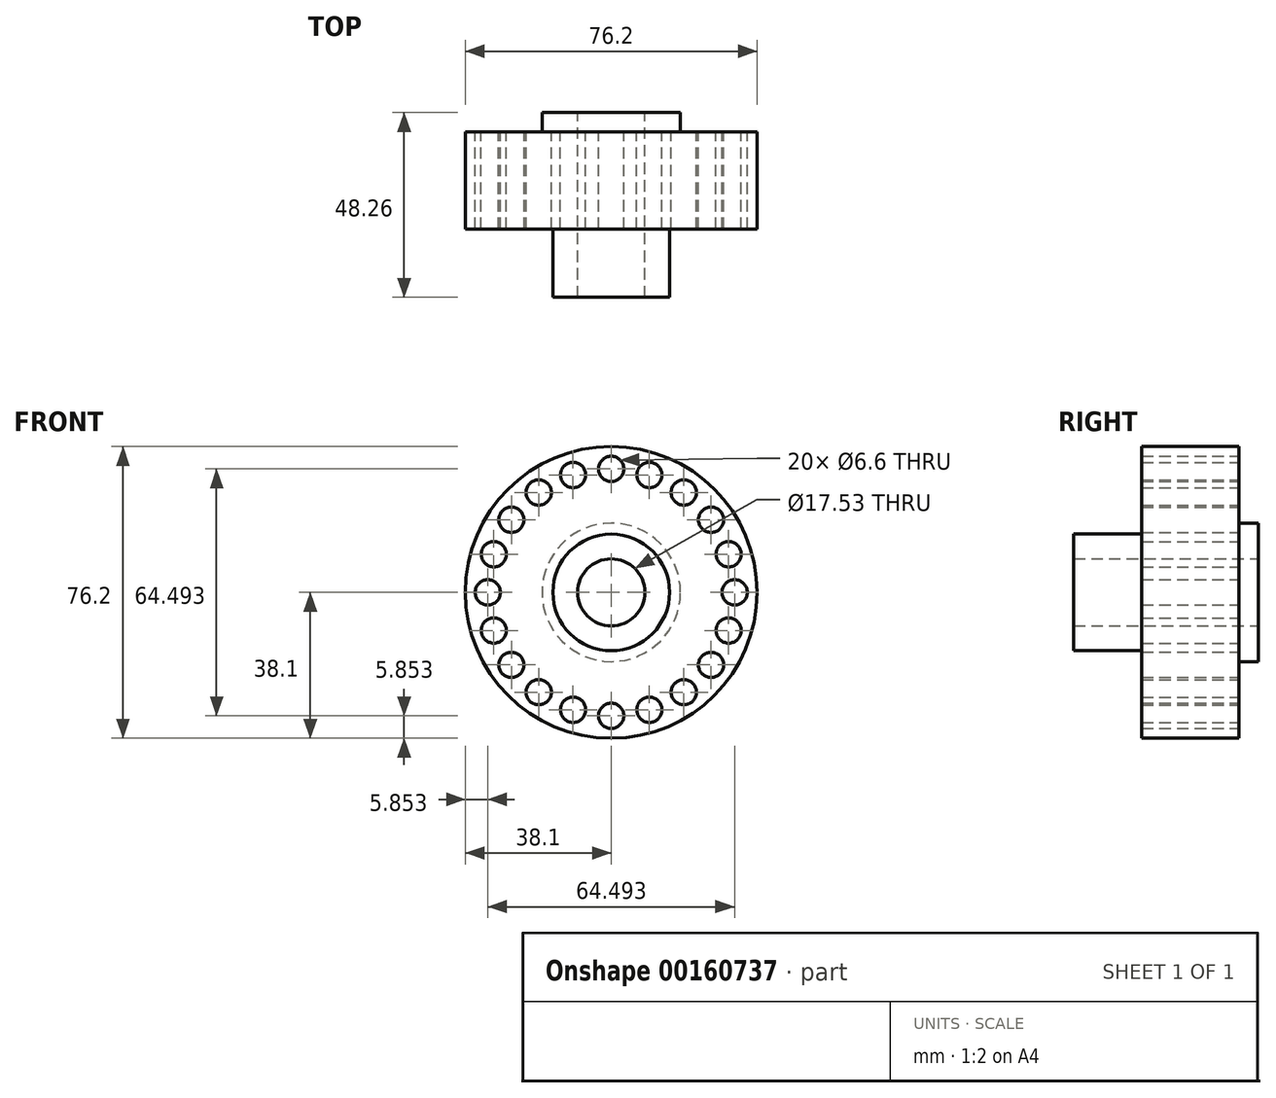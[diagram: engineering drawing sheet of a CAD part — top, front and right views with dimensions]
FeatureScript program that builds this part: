
annotation { "Feature Type Name" : "Feature", "Feature Type Description" : "" }
export const myFeature = defineFeature(function(context is Context, id is Id, definition is map)
    precondition{}
    {
        {
            var Q0;
            Q0=qCreatedBy(makeId("Front.planeOp"),FACE);
            var sketch = newSketch(context, id + "F0", { "sketchPlane" : qUnion([Q0])});
            skCircle(sketch, "E0", {"center": v(0, 0) * mm, "radius": 38.1 * mm});
            skCircle(sketch, "E1", {"center": v(0, 0) * mm, "radius": 8.76 * mm});
            skSolve(sketch);
        }
        {
            var Q0;
            Q0=makeQuery(id+"F0.imprint","IMPRINT",FACE,{"disambiguationData":[TD([[makeQuery(id+"F0.imprint","IMPRINT",EDGE,{"derivedFrom":sQuery(id+"F0.wireOp",EDGE,"E0")}),1.0]])]});
            extrude(context, id + "F1", {"entities" : qUnion([Q0]), "depth" : 25.4 * mm});
        }
        {
            var Q0;
            Q0=makeQuery(id+"F1.opExtrude","CAP_FACE",FACE,{"disambiguationData":[OSD([sQuery(id+"F0.wireOp",EDGE,"E0"),sQuery(id+"F0.wireOp",EDGE,"E1")])],"isStart":true});
            var sketch = newSketch(context, id + "F2", { "sketchPlane" : qUnion([Q0])});
            skPoint(sketch, "E2.center", {"position": v(0, 0) * mm});
            skCircle(sketch, "E3", {"center": v(0, 32.25) * mm, "radius": 3.3 * mm});
            skCircle(sketch, "E4.1.0", {"center": v(-9.96, 30.67) * mm, "radius": 3.3 * mm});
            skCircle(sketch, "E4.2.0", {"center": v(-18.95, 26.09) * mm, "radius": 3.3 * mm});
            skCircle(sketch, "E4.3.0", {"center": v(-26.09, 18.95) * mm, "radius": 3.3 * mm});
            skCircle(sketch, "E4.4.0", {"center": v(-30.67, 9.96) * mm, "radius": 3.3 * mm});
            skCircle(sketch, "E4.5.0", {"center": v(-32.25, 0) * mm, "radius": 3.3 * mm});
            skCircle(sketch, "E4.6.0", {"center": v(-30.67, -9.96) * mm, "radius": 3.3 * mm});
            skCircle(sketch, "E4.7.0", {"center": v(-26.09, -18.95) * mm, "radius": 3.3 * mm});
            skCircle(sketch, "E4.8.0", {"center": v(-18.95, -26.09) * mm, "radius": 3.3 * mm});
            skCircle(sketch, "E4.9.0", {"center": v(-9.96, -30.67) * mm, "radius": 3.3 * mm});
            skCircle(sketch, "E4.10.0", {"center": v(0, -32.25) * mm, "radius": 3.3 * mm});
            skCircle(sketch, "E4.11.0", {"center": v(9.96, -30.67) * mm, "radius": 3.3 * mm});
            skCircle(sketch, "E5.1.12.0", {"center": v(18.95, -26.09) * mm, "radius": 3.3 * mm});
            skCircle(sketch, "E5.1.13.0", {"center": v(26.09, -18.95) * mm, "radius": 3.3 * mm});
            skCircle(sketch, "E5.1.14.0", {"center": v(30.67, -9.96) * mm, "radius": 3.3 * mm});
            skCircle(sketch, "E5.1.15.0", {"center": v(32.25, 0) * mm, "radius": 3.3 * mm});
            skCircle(sketch, "E5.1.16.0", {"center": v(30.67, 9.96) * mm, "radius": 3.3 * mm});
            skCircle(sketch, "E5.1.17.0", {"center": v(26.09, 18.95) * mm, "radius": 3.3 * mm});
            skCircle(sketch, "E5.1.18.0", {"center": v(18.95, 26.09) * mm, "radius": 3.3 * mm});
            skCircle(sketch, "E5.1.19.0", {"center": v(9.96, 30.67) * mm, "radius": 3.3 * mm});
            skSolve(sketch);
        }
        {
            var Q0;
            Q0 = qSketchRegion(id + "F2", true);
            extrude(context, id + "F3", {"entities" : qUnion([Q0]), "operationType" : NewBodyOperationType.REMOVE, "oppositeDirection" : true, "depth" : 30.48 * mm});
        }
        {
            var Q0;
            Q0=makeQuery(id+"F1.opExtrude","CAP_FACE",FACE,{"disambiguationData":[OSD([sQuery(id+"F0.wireOp",EDGE,"E0"),sQuery(id+"F0.wireOp",EDGE,"E1")])],"isStart":false});
            var sketch = newSketch(context, id + "F4", { "sketchPlane" : qUnion([Q0])});
            skCircle(sketch, "E6", {"center": v(0, 0) * mm, "radius": 15.24 * mm});
            skCircle(sketch, "E7", {"center": v(0, 0) * mm, "radius": 8.76 * mm});
            skSolve(sketch);
        }
        {
            var Q0;
            Q0=makeQuery(id+"F4.imprint","IMPRINT",FACE,{"disambiguationData":[TD([[makeQuery(id+"F4.imprint","IMPRINT",EDGE,{"derivedFrom":sQuery(id+"F4.wireOp",EDGE,"E6")}),1.0]])]});
            extrude(context, id + "F5", {"entities" : qUnion([Q0]), "operationType" : NewBodyOperationType.ADD, "depth" : 17.78 * mm});
        }
        {
            var Q0;
            Q0=makeQuery(id+"F1.opExtrude","CAP_FACE",FACE,{"disambiguationData":[OSD([sQuery(id+"F0.wireOp",EDGE,"E0"),sQuery(id+"F0.wireOp",EDGE,"E1")])],"isStart":true});
            var sketch = newSketch(context, id + "F6", { "sketchPlane" : qUnion([Q0])});
            skCircle(sketch, "E8", {"center": v(0, 0) * mm, "radius": 18.08 * mm});
            skCircle(sketch, "E9", {"center": v(0, 0) * mm, "radius": 8.76 * mm});
            skSolve(sketch);
        }
        {
            var Q0;
            Q0=makeQuery(id+"F6.imprint","IMPRINT",FACE,{"disambiguationData":[TD([[makeQuery(id+"F6.imprint","IMPRINT",EDGE,{"derivedFrom":sQuery(id+"F6.wireOp",EDGE,"E8")}),1.0]])]});
            extrude(context, id + "F7", {"entities" : qUnion([Q0]), "operationType" : NewBodyOperationType.ADD, "depth" : 5.08 * mm});
        }
    });
